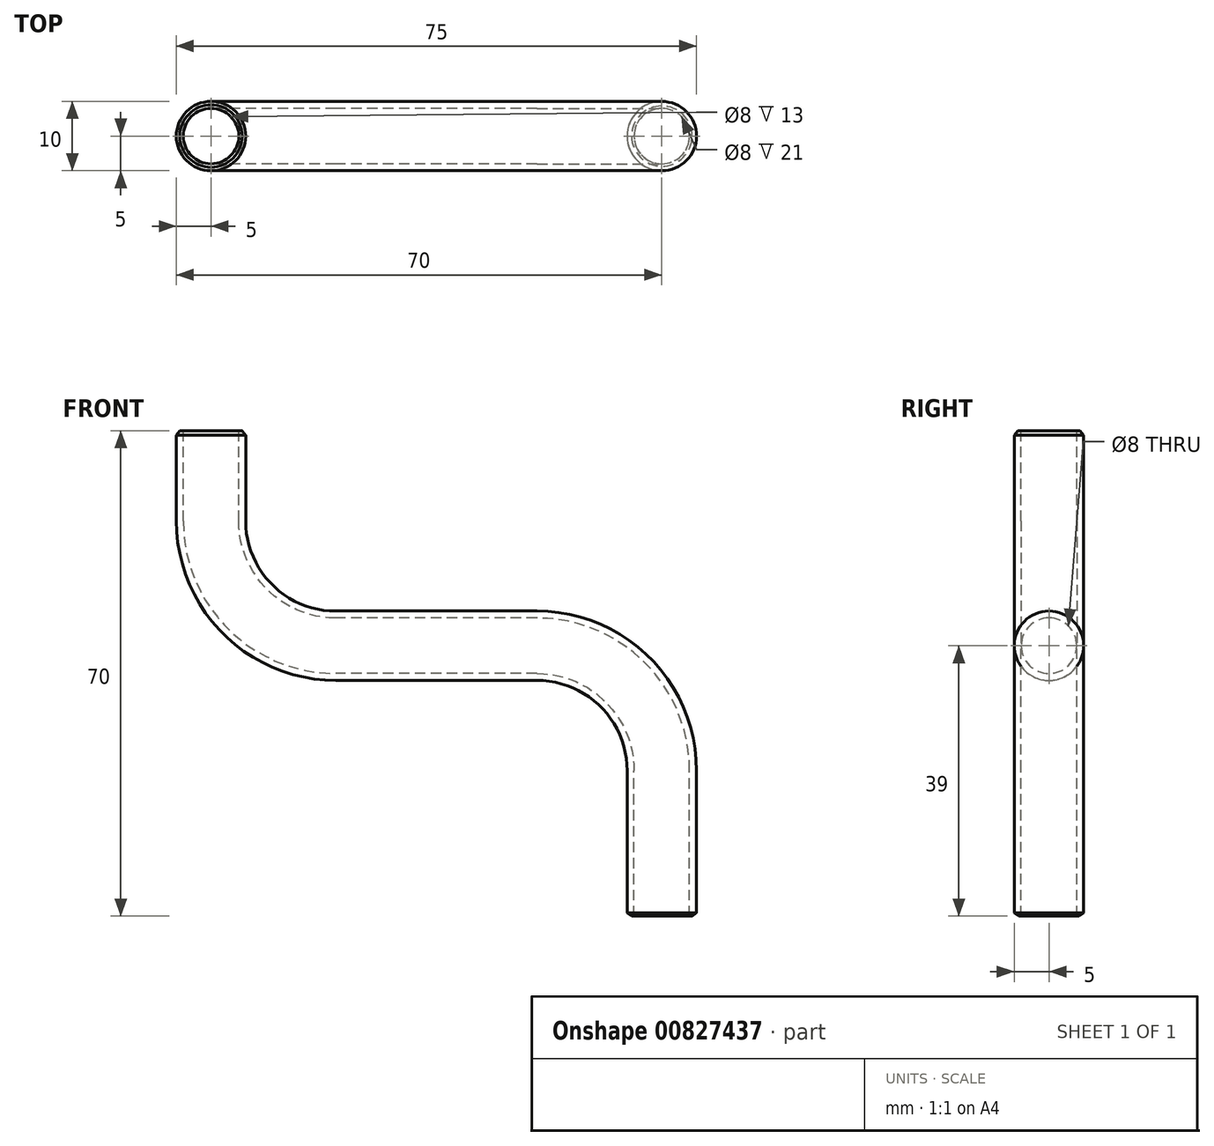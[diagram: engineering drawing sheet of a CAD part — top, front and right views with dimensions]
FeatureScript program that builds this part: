
annotation { "Feature Type Name" : "Feature", "Feature Type Description" : "" }
export const myFeature = defineFeature(function(context is Context, id is Id, definition is map)
    precondition{}
    {
        {
            var Q0;
            Q0=qCreatedBy(makeId("Top.planeOp"),FACE);
            var sketch = newSketch(context, id + "F0", { "sketchPlane" : qUnion([Q0])});
            skCircle(sketch, "E0", {"center": v(0, 0) * mm, "radius": 5 * mm});
            skCircle(sketch, "E1", {"center": v(0, 0) * mm, "radius": 4 * mm});
            skSolve(sketch);
        }
        {
            var Q0;
            Q0=qCreatedBy(makeId("Front.planeOp"),FACE);
            var sketch = newSketch(context, id + "F1", { "sketchPlane" : qUnion([Q0])});
            skArc(sketch, "E2", {"start": v(0, 21) * mm, "mid": v(-5.27, 33.73) * mm, "end": v(-18, 39) * mm});
            skLineSegment(sketch, "E3", {"start": v(-18, 39) * mm, "end": v(-47, 39) * mm});
            skLineSegment(sketch, "E4", {"start": v(0, 21) * mm, "end": v(0, 0) * mm});
            skArc(sketch, "E5", {"start": v(-47, 39) * mm, "mid": v(-59.73, 44.27) * mm, "end": v(-65, 57) * mm});
            skLineSegment(sketch, "E6", {"start": v(-65, 57) * mm, "end": v(-65, 70) * mm});
            skSolve(sketch);
        }
        {
            var Q0;
            Q0=makeQuery(id+"F0.imprint","IMPRINT",FACE,{"disambiguationData":[TD([[makeQuery(id+"F0.imprint","IMPRINT",EDGE,{"derivedFrom":sQuery(id+"F0.wireOp",EDGE,"E0")}),1.0]])]});
            var Q1;
            Q1=sQuery(id+"F1.wireOp",EDGE,"E4");
            var Q2;
            Q2=sQuery(id+"F1.wireOp",EDGE,"E2");
            var Q3;
            Q3=sQuery(id+"F1.wireOp",EDGE,"E3");
            var Q4;
            Q4=sQuery(id+"F1.wireOp",EDGE,"E5");
            var Q5;
            Q5=sQuery(id+"F1.wireOp",EDGE,"E6");
            sweep(context, id + "F2", {"profiles" : qUnion([Q0]), "path" : qUnion([Q1, Q2, Q3, Q4, Q5])});
        }
        {
            var Q0;
            Q0=makeQuery(id+"F2.opSweep","CAP_EDGE",EDGE,{"disambiguationData":[OSD([sQuery(id+"F0.wireOp",EDGE,"E0"),sQuery(id+"F1.wireOp",VERTEX,"E6.end")])],"isStart":false});
            var Q1;
            Q1=makeQuery(id+"F2.opSweep","CAP_EDGE",EDGE,{"disambiguationData":[OSD([sQuery(id+"F0.wireOp",EDGE,"E0"),sQuery(id+"F1.wireOp",VERTEX,"E4.end")])],"isStart":true});
            chamfer(context, id + "F3", {"entities" : qUnion([Q0, Q1]), "chamferType" : ChamferType.OFFSET_ANGLE, "width" : .5 * mm, "oppositeDirection" : false, "angle" : 52.5 * degree, "tangentPropagation" : true});
        }
    });
